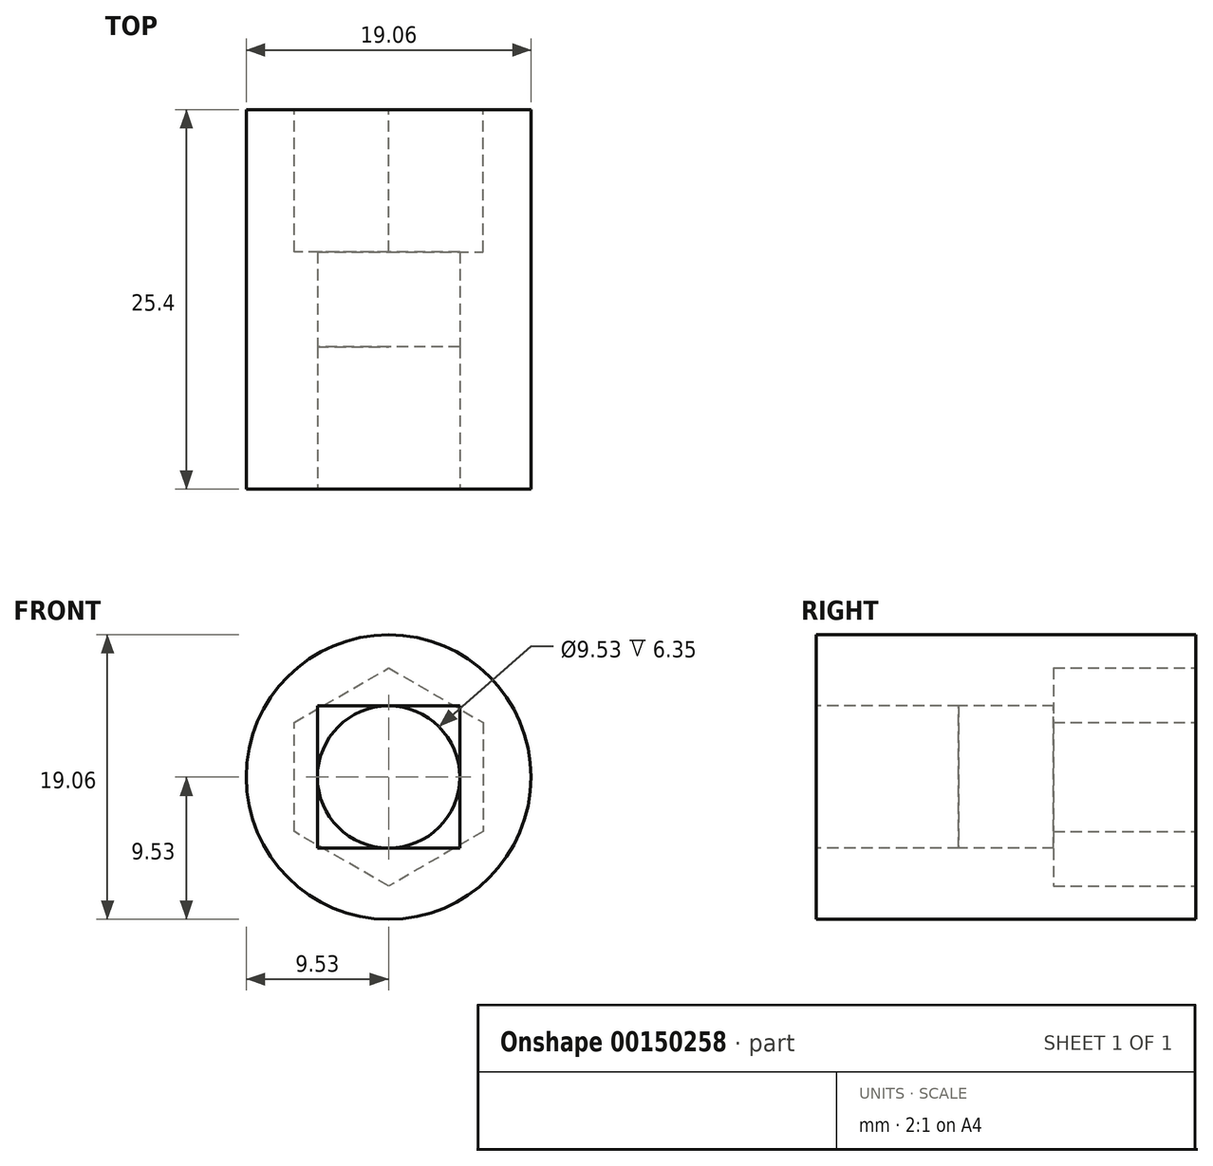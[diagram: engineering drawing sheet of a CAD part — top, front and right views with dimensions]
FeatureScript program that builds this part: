
annotation { "Feature Type Name" : "Feature", "Feature Type Description" : "" }
export const myFeature = defineFeature(function(context is Context, id is Id, definition is map)
    precondition{}
    {
        {
            var Q0;
            Q0=qCreatedBy(makeId("Front.planeOp"),FACE);
            var sketch = newSketch(context, id + "F0", { "sketchPlane" : qUnion([Q0])});
            skCircle(sketch, "E0", {"center": v(0, 0) * mm, "radius": 9.53 * mm});
            skSolve(sketch);
        }
        {
            var Q0;
            Q0 = qSketchRegion(id + "F0", true);
            extrude(context, id + "F1", {"entities" : qUnion([Q0]), "depth" : 25.4 * mm});
        }
        {
            var Q0;
            Q0=makeQuery(id+"F1.opExtrude","CAP_FACE",FACE,{"disambiguationData":[OSD([sQuery(id+"F0.wireOp",EDGE,"E0")])],"isStart":false});
            var sketch = newSketch(context, id + "F2", { "sketchPlane" : qUnion([Q0])});
            skLineSegment(sketch, "E1.bottom", {"start": v(4.76, -4.76) * mm, "end": v(-4.76, -4.76) * mm});
            skLineSegment(sketch, "E1.top", {"start": v(4.76, 4.76) * mm, "end": v(-4.76, 4.76) * mm});
            skLineSegment(sketch, "E1.left", {"start": v(4.76, -4.76) * mm, "end": v(4.76, 4.76) * mm});
            skLineSegment(sketch, "E1.right", {"start": v(-4.76, -4.76) * mm, "end": v(-4.76, 4.76) * mm});
            skPoint(sketch, "E1.middle", {"position": v(0, 0) * mm});
            skCircle(sketch, "E2", {"center": v(0, 0) * mm, "radius": 4.76 * mm});
            skSolve(sketch);
        }
        {
            var Q0;
            {var subQ0=sQuery(id+"F2.wireOp",EDGE,"E2");var subQ1=makeQuery(id+"F2.imprint","INTERSECT",VERTEX,{"derivedFrom":[sQuery(id+"F2.wireOp",EDGE,"E1.top"),subQ0]});Q0=makeQuery(id+"F2.imprint","IMPRINT",FACE,{"disambiguationData":[TD([[makeQuery(id+"F2.imprint","IMPRINT",EDGE,{"disambiguationData":[TD([[subQ1,1.0]])],"derivedFrom":subQ0}),1.0]])]});}
            extrude(context, id + "F3", {"entities" : qUnion([Q0]), "operationType" : NewBodyOperationType.REMOVE, "endBound" : BoundingType.THROUGH_ALL, "oppositeDirection" : true, "depth" : 25.4 * mm});
        }
        {
            var Q0;
            Q0 = qSketchRegion(id + "F2", true);
            extrude(context, id + "F4", {"entities" : qUnion([Q0]), "operationType" : NewBodyOperationType.REMOVE, "oppositeDirection" : true, "depth" : 9.52 * mm});
        }
        {
            var Q0;
            Q0=qCreatedBy(makeId("Front.planeOp"),FACE);
            var sketch = newSketch(context, id + "F5", { "sketchPlane" : qUnion([Q0])});
            skCircle(sketch, "E3.cCircle", {"center": v(0, 0) * mm, "radius": 7.3 * mm, "construction": true});
            skLineSegment(sketch, "E3.0", {"start": v(0, 7.3) * mm, "end": v(6.32, 3.65) * mm});
            skLineSegment(sketch, "E3.1", {"start": v(6.32, 3.65) * mm, "end": v(6.32, -3.65) * mm});
            skLineSegment(sketch, "E3.2", {"start": v(6.32, -3.65) * mm, "end": v(0, -7.3) * mm});
            skLineSegment(sketch, "E3.3", {"start": v(0, -7.3) * mm, "end": v(-6.32, -3.65) * mm});
            skLineSegment(sketch, "E3.4", {"start": v(-6.32, -3.65) * mm, "end": v(-6.32, 3.65) * mm});
            skLineSegment(sketch, "E3.5", {"start": v(-6.32, 3.65) * mm, "end": v(0, 7.3) * mm});
            skSolve(sketch);
        }
        {
            var Q0;
            Q0 = qSketchRegion(id + "F5", true);
            extrude(context, id + "F6", {"entities" : qUnion([Q0]), "operationType" : NewBodyOperationType.REMOVE, "depth" : 9.52 * mm});
        }
    });
